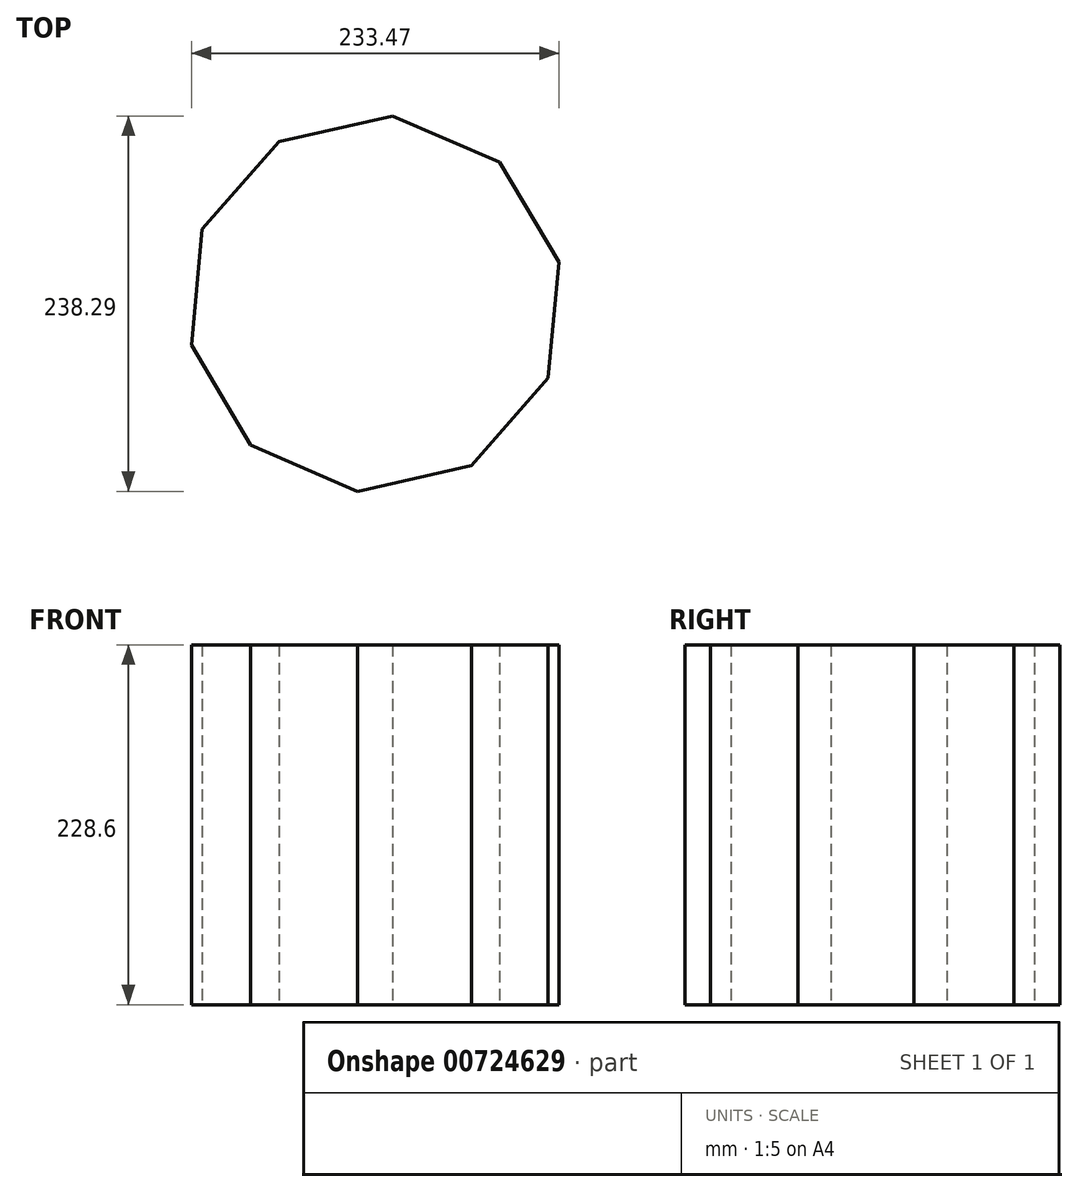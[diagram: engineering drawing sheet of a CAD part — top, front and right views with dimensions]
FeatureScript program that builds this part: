
annotation { "Feature Type Name" : "Feature", "Feature Type Description" : "" }
export const myFeature = defineFeature(function(context is Context, id is Id, definition is map)
    precondition{}
    {
        {
            var Q0;
            Q0=qCreatedBy(makeId("Top.planeOp"),FACE);
            var sketch = newSketch(context, id + "F0", { "sketchPlane" : qUnion([Q0])});
            skCircle(sketch, "E0.cCircle", {"center": v(-137.35, -117.03) * mm, "radius": 113.8 * mm, "construction": true});
            skLineSegment(sketch, "E0.0", {"start": v(-27.45, -164.37) * mm, "end": v(-76.26, -219.92) * mm});
            skLineSegment(sketch, "E0.1", {"start": v(-76.26, -219.92) * mm, "end": v(-148.4, -236.17) * mm});
            skLineSegment(sketch, "E0.2", {"start": v(-148.4, -236.17) * mm, "end": v(-216.33, -206.91) * mm});
            skLineSegment(sketch, "E0.3", {"start": v(-216.33, -206.91) * mm, "end": v(-254.08, -143.32) * mm});
            skLineSegment(sketch, "E0.4", {"start": v(-254.08, -143.32) * mm, "end": v(-247.24, -69.69) * mm});
            skLineSegment(sketch, "E0.5", {"start": v(-247.24, -69.69) * mm, "end": v(-198.43, -14.13) * mm});
            skLineSegment(sketch, "E0.6", {"start": v(-198.43, -14.13) * mm, "end": v(-126.28, 2.12) * mm});
            skLineSegment(sketch, "E0.7", {"start": v(-126.28, 2.12) * mm, "end": v(-58.36, -27.14) * mm});
            skLineSegment(sketch, "E0.8", {"start": v(-58.36, -27.14) * mm, "end": v(-20.61, -90.73) * mm});
            skLineSegment(sketch, "E0.9", {"start": v(-20.61, -90.73) * mm, "end": v(-27.45, -164.37) * mm});
            skPoint(sketch, "E0.0.midPoint", {"position": v(-51.86, -192.14) * mm});
            skSolve(sketch);
        }
        {
            var Q0;
            Q0=makeQuery(id+"F0.imprint","IMPRINT",FACE,{"disambiguationData":[TD([[makeQuery(id+"F0.imprint","IMPRINT",EDGE,{"derivedFrom":sQuery(id+"F0.wireOp",EDGE,"E0.0")}),-1.0]])]});
            extrude(context, id + "F1", {"entities" : qUnion([Q0]), "depth" : 228.6 * mm, "offsetDistance" : 25.4 * mm});
        }
    });
